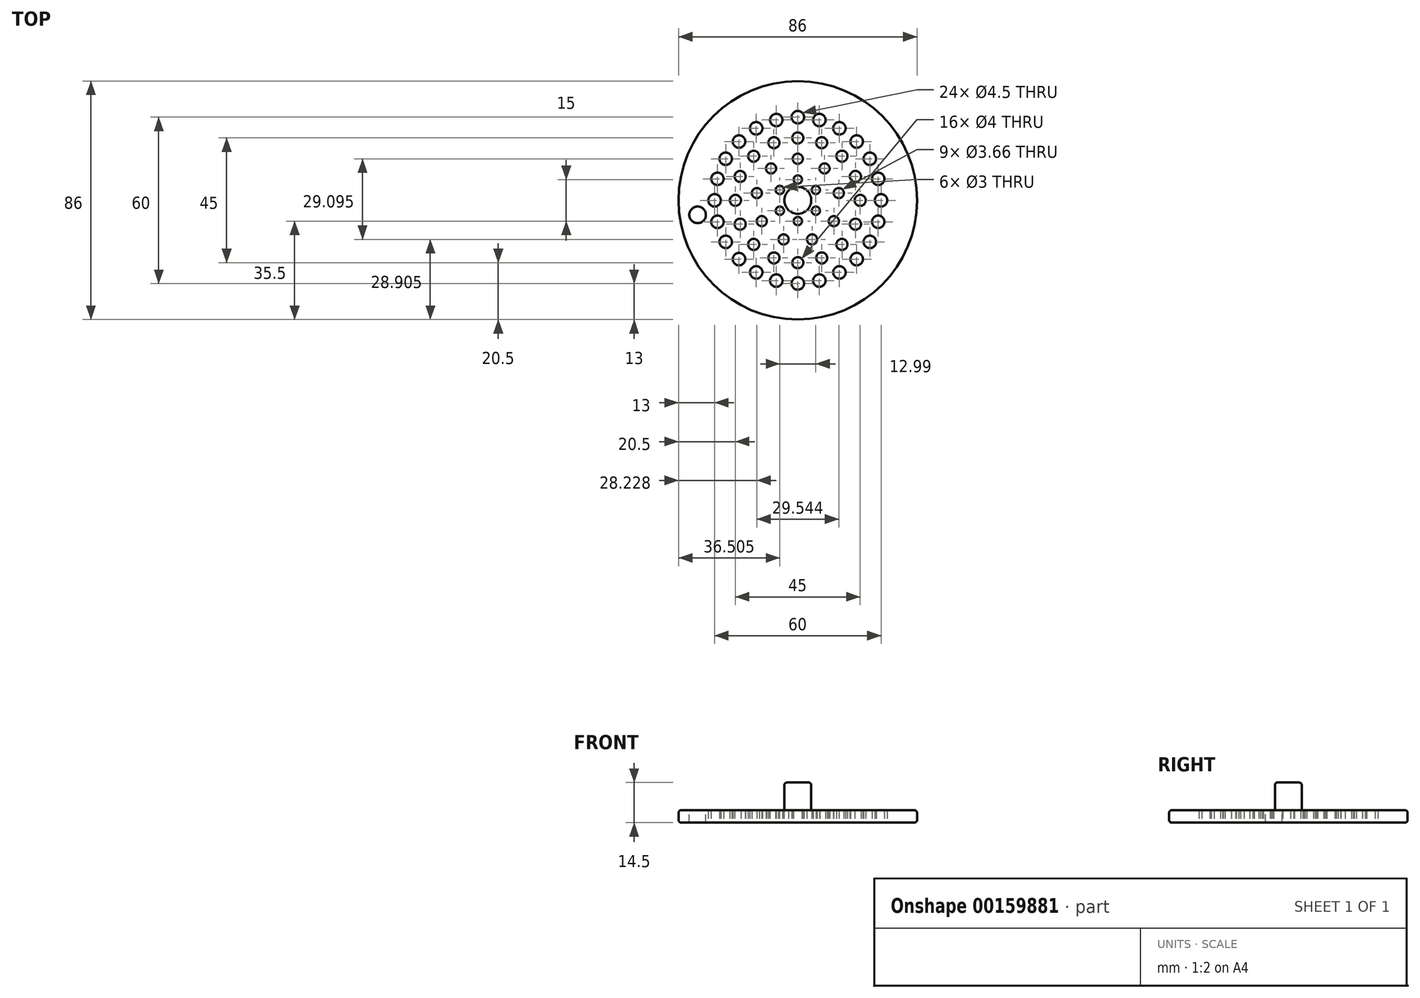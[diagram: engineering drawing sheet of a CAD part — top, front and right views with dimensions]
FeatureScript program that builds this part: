
annotation { "Feature Type Name" : "Feature", "Feature Type Description" : "" }
export const myFeature = defineFeature(function(context is Context, id is Id, definition is map)
    precondition{}
    {
        {
            var Q0;
            Q0=qCreatedBy(makeId("Top.planeOp"),FACE);
            var sketch = newSketch(context, id + "F0", { "sketchPlane" : qUnion([Q0])});
            skCircle(sketch, "E0", {"center": v(0, 0) * mm, "radius": 43 * mm});
            skSolve(sketch);
        }
        {
            var Q0;
            Q0=makeQuery(id+"F0.imprint","IMPRINT",FACE,{"disambiguationData":[TD([[makeQuery(id+"F0.imprint","IMPRINT",EDGE,{"derivedFrom":sQuery(id+"F0.wireOp",EDGE,"E0")}),1.0]])]});
            var sketch = newSketch(context, id + "F1", { "sketchPlane" : qUnion([Q0])});
            skCircle(sketch, "E1", {"center": v(0, 0) * mm, "radius": 7.5 * mm, "construction": true});
            skCircle(sketch, "E2", {"center": v(0, 7.5) * mm, "radius": 1.5 * mm});
            skCircle(sketch, "E3.1.1", {"center": v(-6.5, 3.75) * mm, "radius": 1.5 * mm});
            skCircle(sketch, "E3.2.1", {"center": v(-6.5, -3.75) * mm, "radius": 1.5 * mm});
            skCircle(sketch, "E3.3.1", {"center": v(0, -7.5) * mm, "radius": 1.5 * mm});
            skCircle(sketch, "E3.4.1", {"center": v(6.5, -3.75) * mm, "radius": 1.5 * mm});
            skCircle(sketch, "E3.5.1", {"center": v(6.5, 3.75) * mm, "radius": 1.5 * mm});
            skSolve(sketch);
        }
        {
            var Q0;
            Q0=makeQuery(id+"F0.imprint","IMPRINT",FACE,{"disambiguationData":[TD([[makeQuery(id+"F0.imprint","IMPRINT",EDGE,{"derivedFrom":sQuery(id+"F0.wireOp",EDGE,"E0")}),1.0]])]});
            var sketch = newSketch(context, id + "F2", { "sketchPlane" : qUnion([Q0])});
            skCircle(sketch, "E4", {"center": v(0, 0) * mm, "radius": 15 * mm, "construction": true});
            skCircle(sketch, "E5", {"center": v(0, 15) * mm, "radius": 1.83 * mm});
            skCircle(sketch, "E6.1.0", {"center": v(-9.64, 11.5) * mm, "radius": 1.83 * mm});
            skCircle(sketch, "E6.2.0", {"center": v(-14.77, 2.6) * mm, "radius": 1.83 * mm});
            skCircle(sketch, "E6.3.0", {"center": v(-13, -7.5) * mm, "radius": 1.83 * mm});
            skCircle(sketch, "E6.4.0", {"center": v(-5.13, -14.1) * mm, "radius": 1.83 * mm});
            skCircle(sketch, "E6.5.0", {"center": v(5.13, -14.1) * mm, "radius": 1.83 * mm});
            skCircle(sketch, "E6.6.0", {"center": v(13, -7.5) * mm, "radius": 1.83 * mm});
            skCircle(sketch, "E6.7.0", {"center": v(14.77, 2.6) * mm, "radius": 1.83 * mm});
            skCircle(sketch, "E6.8.0", {"center": v(9.64, 11.5) * mm, "radius": 1.83 * mm});
            skSolve(sketch);
        }
        {
            var Q0;
            Q0=makeQuery(id+"F0.imprint","IMPRINT",FACE,{"disambiguationData":[TD([[makeQuery(id+"F0.imprint","IMPRINT",EDGE,{"derivedFrom":sQuery(id+"F0.wireOp",EDGE,"E0")}),1.0]])]});
            var sketch = newSketch(context, id + "F3", { "sketchPlane" : qUnion([Q0])});
            skCircle(sketch, "E7", {"center": v(0, 0) * mm, "radius": 22.5 * mm, "construction": true});
            skCircle(sketch, "E8", {"center": v(0, 22.5) * mm, "radius": 2 * mm});
            skCircle(sketch, "E9.1.0", {"center": v(-8.61, 20.79) * mm, "radius": 2 * mm});
            skCircle(sketch, "E9.2.0", {"center": v(-15.9, 15.9) * mm, "radius": 2 * mm});
            skCircle(sketch, "E9.3.0", {"center": v(-20.79, 8.61) * mm, "radius": 2 * mm});
            skCircle(sketch, "E9.4.0", {"center": v(-22.5, 0) * mm, "radius": 2 * mm});
            skCircle(sketch, "E9.5.0", {"center": v(-20.79, -8.61) * mm, "radius": 2 * mm});
            skCircle(sketch, "E9.6.0", {"center": v(-15.9, -15.9) * mm, "radius": 2 * mm});
            skCircle(sketch, "E9.7.0", {"center": v(-8.61, -20.79) * mm, "radius": 2 * mm});
            skCircle(sketch, "E9.8.0", {"center": v(0, -22.5) * mm, "radius": 2 * mm});
            skCircle(sketch, "E9.9.0", {"center": v(8.61, -20.79) * mm, "radius": 2 * mm});
            skCircle(sketch, "E9.10.0", {"center": v(15.9, -15.9) * mm, "radius": 2 * mm});
            skCircle(sketch, "E9.11.0", {"center": v(20.79, -8.61) * mm, "radius": 2 * mm});
            skCircle(sketch, "E9.12.0", {"center": v(22.5, 0) * mm, "radius": 2 * mm});
            skCircle(sketch, "E9.13.0", {"center": v(20.79, 8.61) * mm, "radius": 2 * mm});
            skCircle(sketch, "E9.14.0", {"center": v(15.9, 15.9) * mm, "radius": 2 * mm});
            skCircle(sketch, "E9.15.0", {"center": v(8.61, 20.79) * mm, "radius": 2 * mm});
            skSolve(sketch);
        }
        {
            var Q0;
            Q0=makeQuery(id+"F0.imprint","IMPRINT",FACE,{"disambiguationData":[TD([[makeQuery(id+"F0.imprint","IMPRINT",EDGE,{"derivedFrom":sQuery(id+"F0.wireOp",EDGE,"E0")}),1.0]])]});
            var sketch = newSketch(context, id + "F4", { "sketchPlane" : qUnion([Q0])});
            skCircle(sketch, "E10", {"center": v(0, 0) * mm, "radius": 30 * mm, "construction": true});
            skCircle(sketch, "E11", {"center": v(0, 30) * mm, "radius": 2.25 * mm});
            skCircle(sketch, "E12.1.0", {"center": v(-7.76, 28.98) * mm, "radius": 2.25 * mm});
            skCircle(sketch, "E12.2.0", {"center": v(-15, 25.98) * mm, "radius": 2.25 * mm});
            skCircle(sketch, "E13.1.3.0", {"center": v(-21.21, 21.21) * mm, "radius": 2.25 * mm});
            skCircle(sketch, "E13.1.4.0", {"center": v(-25.98, 15) * mm, "radius": 2.25 * mm});
            skCircle(sketch, "E13.1.5.0", {"center": v(-28.98, 7.76) * mm, "radius": 2.25 * mm});
            skCircle(sketch, "E13.1.6.0", {"center": v(-30, 0) * mm, "radius": 2.25 * mm});
            skCircle(sketch, "E13.1.7.0", {"center": v(-28.98, -7.76) * mm, "radius": 2.25 * mm});
            skCircle(sketch, "E13.1.8.0", {"center": v(-25.98, -15) * mm, "radius": 2.25 * mm});
            skCircle(sketch, "E13.1.9.0", {"center": v(-21.21, -21.21) * mm, "radius": 2.25 * mm});
            skCircle(sketch, "E13.1.10.0", {"center": v(-15, -25.98) * mm, "radius": 2.25 * mm});
            skCircle(sketch, "E13.1.11.0", {"center": v(-7.76, -28.98) * mm, "radius": 2.25 * mm});
            skCircle(sketch, "E13.1.12.0", {"center": v(0, -30) * mm, "radius": 2.25 * mm});
            skCircle(sketch, "E13.1.13.0", {"center": v(7.76, -28.98) * mm, "radius": 2.25 * mm});
            skCircle(sketch, "E13.1.14.0", {"center": v(15, -25.98) * mm, "radius": 2.25 * mm});
            skCircle(sketch, "E13.1.15.0", {"center": v(21.21, -21.21) * mm, "radius": 2.25 * mm});
            skCircle(sketch, "E13.1.16.0", {"center": v(25.98, -15) * mm, "radius": 2.25 * mm});
            skCircle(sketch, "E13.1.17.0", {"center": v(28.98, -7.76) * mm, "radius": 2.25 * mm});
            skCircle(sketch, "E13.1.18.0", {"center": v(30, 0) * mm, "radius": 2.25 * mm});
            skCircle(sketch, "E13.1.19.0", {"center": v(28.98, 7.76) * mm, "radius": 2.25 * mm});
            skCircle(sketch, "E13.1.20.0", {"center": v(25.98, 15) * mm, "radius": 2.25 * mm});
            skCircle(sketch, "E13.1.21.0", {"center": v(21.21, 21.21) * mm, "radius": 2.25 * mm});
            skCircle(sketch, "E13.1.22.0", {"center": v(15, 25.98) * mm, "radius": 2.25 * mm});
            skCircle(sketch, "E13.1.23.0", {"center": v(7.76, 28.98) * mm, "radius": 2.25 * mm});
            skSolve(sketch);
        }
        {
            var Q0;
            Q0=qSketchRegion(id+"F4",true);
            extrude(context, id + "F5", {"entities" : qUnion([Q0]), "depth" : 5 * mm});
        }
        {
            var Q0;
            Q0=qSketchRegion(id+"F3",true);
            extrude(context, id + "F6", {"entities" : qUnion([Q0]), "depth" : 5 * mm});
        }
        {
            var Q0;
            Q0=qSketchRegion(id+"F2",true);
            extrude(context, id + "F7", {"entities" : qUnion([Q0]), "depth" : 5 * mm});
        }
        {
            var Q0;
            Q0=qSketchRegion(id+"F1",true);
            extrude(context, id + "F8", {"entities" : qUnion([Q0]), "depth" : 5 * mm});
        }
        {
            var Q0;
            Q0=qSketchRegion(id+"F0",true);
            extrude(context, id + "F9", {"entities" : qUnion([Q0]), "depth" : 4.5 * mm});
        }
        {
            var Q0;
            Q0=makeQuery(id+"F5.opExtrude","SWEPT_BODY",BODY,{"disambiguationData":[OSD([sQuery(id+"F4.wireOp",EDGE,"E11")])]});
            var Q1;
            Q1=makeQuery(id+"F5.opExtrude","SWEPT_BODY",BODY,{"disambiguationData":[OSD([sQuery(id+"F4.wireOp",EDGE,"E13.1.3.0")])]});
            var Q2;
            Q2=makeQuery(id+"F5.opExtrude","SWEPT_BODY",BODY,{"disambiguationData":[OSD([sQuery(id+"F4.wireOp",EDGE,"E13.1.7.0")])]});
            var Q3;
            Q3=makeQuery(id+"F5.opExtrude","SWEPT_BODY",BODY,{"disambiguationData":[OSD([sQuery(id+"F4.wireOp",EDGE,"E12.1.0")])]});
            var Q4;
            Q4=makeQuery(id+"F5.opExtrude","SWEPT_BODY",BODY,{"disambiguationData":[OSD([sQuery(id+"F4.wireOp",EDGE,"E12.2.0")])]});
            var Q5;
            Q5=makeQuery(id+"F5.opExtrude","SWEPT_BODY",BODY,{"disambiguationData":[OSD([sQuery(id+"F4.wireOp",EDGE,"E13.1.4.0")])]});
            var Q6;
            Q6=makeQuery(id+"F5.opExtrude","SWEPT_BODY",BODY,{"disambiguationData":[OSD([sQuery(id+"F4.wireOp",EDGE,"E13.1.5.0")])]});
            var Q7;
            Q7=makeQuery(id+"F5.opExtrude","SWEPT_BODY",BODY,{"disambiguationData":[OSD([sQuery(id+"F4.wireOp",EDGE,"E13.1.6.0")])]});
            var Q8;
            Q8=makeQuery(id+"F5.opExtrude","SWEPT_BODY",BODY,{"disambiguationData":[OSD([sQuery(id+"F4.wireOp",EDGE,"E13.1.8.0")])]});
            var Q9;
            Q9=makeQuery(id+"F5.opExtrude","SWEPT_BODY",BODY,{"disambiguationData":[OSD([sQuery(id+"F4.wireOp",EDGE,"E13.1.9.0")])]});
            var Q10;
            Q10=makeQuery(id+"F5.opExtrude","SWEPT_BODY",BODY,{"disambiguationData":[OSD([sQuery(id+"F4.wireOp",EDGE,"E13.1.10.0")])]});
            var Q11;
            Q11=makeQuery(id+"F5.opExtrude","SWEPT_BODY",BODY,{"disambiguationData":[OSD([sQuery(id+"F4.wireOp",EDGE,"E13.1.11.0")])]});
            var Q12;
            Q12=makeQuery(id+"F5.opExtrude","SWEPT_BODY",BODY,{"disambiguationData":[OSD([sQuery(id+"F4.wireOp",EDGE,"E13.1.12.0")])]});
            var Q13;
            Q13=makeQuery(id+"F5.opExtrude","SWEPT_BODY",BODY,{"disambiguationData":[OSD([sQuery(id+"F4.wireOp",EDGE,"E13.1.13.0")])]});
            var Q14;
            Q14=makeQuery(id+"F5.opExtrude","SWEPT_BODY",BODY,{"disambiguationData":[OSD([sQuery(id+"F4.wireOp",EDGE,"E13.1.14.0")])]});
            var Q15;
            Q15=makeQuery(id+"F5.opExtrude","SWEPT_BODY",BODY,{"disambiguationData":[OSD([sQuery(id+"F4.wireOp",EDGE,"E13.1.15.0")])]});
            var Q16;
            Q16=makeQuery(id+"F5.opExtrude","SWEPT_BODY",BODY,{"disambiguationData":[OSD([sQuery(id+"F4.wireOp",EDGE,"E13.1.16.0")])]});
            var Q17;
            Q17=makeQuery(id+"F5.opExtrude","SWEPT_BODY",BODY,{"disambiguationData":[OSD([sQuery(id+"F4.wireOp",EDGE,"E13.1.17.0")])]});
            var Q18;
            Q18=makeQuery(id+"F5.opExtrude","SWEPT_BODY",BODY,{"disambiguationData":[OSD([sQuery(id+"F4.wireOp",EDGE,"E13.1.18.0")])]});
            var Q19;
            Q19=makeQuery(id+"F5.opExtrude","SWEPT_BODY",BODY,{"disambiguationData":[OSD([sQuery(id+"F4.wireOp",EDGE,"E13.1.19.0")])]});
            var Q20;
            Q20=makeQuery(id+"F5.opExtrude","SWEPT_BODY",BODY,{"disambiguationData":[OSD([sQuery(id+"F4.wireOp",EDGE,"E13.1.20.0")])]});
            var Q21;
            Q21=makeQuery(id+"F5.opExtrude","SWEPT_BODY",BODY,{"disambiguationData":[OSD([sQuery(id+"F4.wireOp",EDGE,"E13.1.21.0")])]});
            var Q22;
            Q22=makeQuery(id+"F5.opExtrude","SWEPT_BODY",BODY,{"disambiguationData":[OSD([sQuery(id+"F4.wireOp",EDGE,"E13.1.22.0")])]});
            var Q23;
            Q23=makeQuery(id+"F5.opExtrude","SWEPT_BODY",BODY,{"disambiguationData":[OSD([sQuery(id+"F4.wireOp",EDGE,"E13.1.23.0")])]});
            var Q24;
            Q24=makeQuery(id+"F6.opExtrude","SWEPT_BODY",BODY,{"disambiguationData":[OSD([sQuery(id+"F3.wireOp",EDGE,"E9.15.0")])]});
            var Q25;
            Q25=makeQuery(id+"F6.opExtrude","SWEPT_BODY",BODY,{"disambiguationData":[OSD([sQuery(id+"F3.wireOp",EDGE,"E8")])]});
            var Q26;
            Q26=makeQuery(id+"F6.opExtrude","SWEPT_BODY",BODY,{"disambiguationData":[OSD([sQuery(id+"F3.wireOp",EDGE,"E9.1.0")])]});
            var Q27;
            Q27=makeQuery(id+"F6.opExtrude","SWEPT_BODY",BODY,{"disambiguationData":[OSD([sQuery(id+"F3.wireOp",EDGE,"E9.2.0")])]});
            var Q28;
            Q28=makeQuery(id+"F6.opExtrude","SWEPT_BODY",BODY,{"disambiguationData":[OSD([sQuery(id+"F3.wireOp",EDGE,"E9.3.0")])]});
            var Q29;
            Q29=makeQuery(id+"F6.opExtrude","SWEPT_BODY",BODY,{"disambiguationData":[OSD([sQuery(id+"F3.wireOp",EDGE,"E9.4.0")])]});
            var Q30;
            Q30=makeQuery(id+"F6.opExtrude","SWEPT_BODY",BODY,{"disambiguationData":[OSD([sQuery(id+"F3.wireOp",EDGE,"E9.5.0")])]});
            var Q31;
            Q31=makeQuery(id+"F6.opExtrude","SWEPT_BODY",BODY,{"disambiguationData":[OSD([sQuery(id+"F3.wireOp",EDGE,"E9.6.0")])]});
            var Q32;
            Q32=makeQuery(id+"F6.opExtrude","SWEPT_BODY",BODY,{"disambiguationData":[OSD([sQuery(id+"F3.wireOp",EDGE,"E9.7.0")])]});
            var Q33;
            Q33=makeQuery(id+"F6.opExtrude","SWEPT_BODY",BODY,{"disambiguationData":[OSD([sQuery(id+"F3.wireOp",EDGE,"E9.8.0")])]});
            var Q34;
            Q34=makeQuery(id+"F6.opExtrude","SWEPT_BODY",BODY,{"disambiguationData":[OSD([sQuery(id+"F3.wireOp",EDGE,"E9.9.0")])]});
            var Q35;
            Q35=makeQuery(id+"F6.opExtrude","SWEPT_BODY",BODY,{"disambiguationData":[OSD([sQuery(id+"F3.wireOp",EDGE,"E9.10.0")])]});
            var Q36;
            Q36=makeQuery(id+"F6.opExtrude","SWEPT_BODY",BODY,{"disambiguationData":[OSD([sQuery(id+"F3.wireOp",EDGE,"E9.11.0")])]});
            var Q37;
            Q37=makeQuery(id+"F6.opExtrude","SWEPT_BODY",BODY,{"disambiguationData":[OSD([sQuery(id+"F3.wireOp",EDGE,"E9.12.0")])]});
            var Q38;
            Q38=makeQuery(id+"F6.opExtrude","SWEPT_BODY",BODY,{"disambiguationData":[OSD([sQuery(id+"F3.wireOp",EDGE,"E9.13.0")])]});
            var Q39;
            Q39=makeQuery(id+"F6.opExtrude","SWEPT_BODY",BODY,{"disambiguationData":[OSD([sQuery(id+"F3.wireOp",EDGE,"E9.14.0")])]});
            var Q40;
            Q40=makeQuery(id+"F7.opExtrude","SWEPT_BODY",BODY,{"disambiguationData":[OSD([sQuery(id+"F2.wireOp",EDGE,"E6.8.0")])]});
            var Q41;
            Q41=makeQuery(id+"F7.opExtrude","SWEPT_BODY",BODY,{"disambiguationData":[OSD([sQuery(id+"F2.wireOp",EDGE,"E6.7.0")])]});
            var Q42;
            Q42=makeQuery(id+"F7.opExtrude","SWEPT_BODY",BODY,{"disambiguationData":[OSD([sQuery(id+"F2.wireOp",EDGE,"E6.6.0")])]});
            var Q43;
            Q43=makeQuery(id+"F7.opExtrude","SWEPT_BODY",BODY,{"disambiguationData":[OSD([sQuery(id+"F2.wireOp",EDGE,"E6.5.0")])]});
            var Q44;
            Q44=makeQuery(id+"F7.opExtrude","SWEPT_BODY",BODY,{"disambiguationData":[OSD([sQuery(id+"F2.wireOp",EDGE,"E6.4.0")])]});
            var Q45;
            Q45=makeQuery(id+"F7.opExtrude","SWEPT_BODY",BODY,{"disambiguationData":[OSD([sQuery(id+"F2.wireOp",EDGE,"E6.3.0")])]});
            var Q46;
            Q46=makeQuery(id+"F7.opExtrude","SWEPT_BODY",BODY,{"disambiguationData":[OSD([sQuery(id+"F2.wireOp",EDGE,"E6.2.0")])]});
            var Q47;
            Q47=makeQuery(id+"F7.opExtrude","SWEPT_BODY",BODY,{"disambiguationData":[OSD([sQuery(id+"F2.wireOp",EDGE,"E6.1.0")])]});
            var Q48;
            Q48=makeQuery(id+"F7.opExtrude","SWEPT_BODY",BODY,{"disambiguationData":[OSD([sQuery(id+"F2.wireOp",EDGE,"E5")])]});
            var Q49;
            Q49=makeQuery(id+"F8.opExtrude","SWEPT_BODY",BODY,{"disambiguationData":[OSD([sQuery(id+"F1.wireOp",EDGE,"E2")])]});
            var Q50;
            Q50=makeQuery(id+"F8.opExtrude","SWEPT_BODY",BODY,{"disambiguationData":[OSD([sQuery(id+"F1.wireOp",EDGE,"E3.5.1")])]});
            var Q51;
            Q51=makeQuery(id+"F8.opExtrude","SWEPT_BODY",BODY,{"disambiguationData":[OSD([sQuery(id+"F1.wireOp",EDGE,"E3.4.1")])]});
            var Q52;
            Q52=makeQuery(id+"F8.opExtrude","SWEPT_BODY",BODY,{"disambiguationData":[OSD([sQuery(id+"F1.wireOp",EDGE,"E3.3.1")])]});
            var Q53;
            Q53=makeQuery(id+"F8.opExtrude","SWEPT_BODY",BODY,{"disambiguationData":[OSD([sQuery(id+"F1.wireOp",EDGE,"E3.2.1")])]});
            var Q54;
            Q54=makeQuery(id+"F8.opExtrude","SWEPT_BODY",BODY,{"disambiguationData":[OSD([sQuery(id+"F1.wireOp",EDGE,"E3.1.1")])]});
            var Q55;
            Q55=makeQuery(id+"F9.opExtrude","SWEPT_BODY",BODY,{"disambiguationData":[OSD([sQuery(id+"F0.wireOp",EDGE,"E0")])]});
            booleanBodies(context, id + "F10", {"operationType" : BooleanOperationType.SUBTRACTION, "tools" : qUnion([Q0, Q1, Q2, Q3, Q4, Q5, Q6, Q7, Q8, Q9, Q10, Q11, Q12, Q13, Q14, Q15, Q16, Q17, Q18, Q19, Q20, Q21, Q22, Q23, Q24, Q25, Q26, Q27, Q28, Q29, Q30, Q31, Q32, Q33, Q34, Q35, Q36, Q37, Q38, Q39, Q40, Q41, Q42, Q43, Q44, Q45, Q46, Q47, Q48, Q49, Q50, Q51, Q52, Q53, Q54]), "targets" : qUnion([Q55])});
        }
        {
            var Q0;
            Q0=makeQuery(id+"F9.opExtrude","CAP_EDGE",EDGE,{"disambiguationData":[OSD([sQuery(id+"F0.wireOp",EDGE,"E0")])],"isStart":true});
            var Q1;
            Q1=makeQuery(id+"F9.opExtrude","CAP_EDGE",EDGE,{"disambiguationData":[OSD([sQuery(id+"F0.wireOp",EDGE,"E0")])],"isStart":false});
            fillet(context, id + "F11", {"entities" : qUnion([Q0, Q1]), "radius" : 1 * mm, "tangentPropagation" : true, "allowEdgeOverflow" : false});
        }
        {
            var Q0;
            Q0=makeQuery(id+"F9.opExtrude","CAP_FACE",FACE,{"disambiguationData":[OSD([sQuery(id+"F0.wireOp",EDGE,"E0")])],"isStart":false});
            var sketch = newSketch(context, id + "F12", { "sketchPlane" : qUnion([Q0])});
            skCircle(sketch, "E14", {"center": v(0, 0) * mm, "radius": 4.85 * mm});
            skSolve(sketch);
        }
        {
            var Q0;
            Q0=makeQuery(id+"F12.imprint","IMPRINT",FACE,{"disambiguationData":[TD([[makeQuery(id+"F12.imprint","IMPRINT",EDGE,{"derivedFrom":sQuery(id+"F12.wireOp",EDGE,"E14")}),1.0]])]});
            extrude(context, id + "F13", {"entities" : qUnion([Q0]), "operationType" : NewBodyOperationType.ADD, "depth" : 10 * mm});
        }
        {
            var Q0;
            Q0=makeQuery(id+"F13.opExtrude","CAP_EDGE",EDGE,{"disambiguationData":[OSD([sQuery(id+"F12.wireOp",EDGE,"E14")])],"isStart":false});
            fillet(context, id + "F14", {"entities" : qUnion([Q0]), "radius" : 1 * mm, "tangentPropagation" : true, "allowEdgeOverflow" : false});
        }
        {
            var Q0;
            Q0=makeQuery(id+"F9.opExtrude","CAP_FACE",FACE,{"disambiguationData":[OSD([sQuery(id+"F0.wireOp",EDGE,"E0")])],"isStart":false});
            var sketch = newSketch(context, id + "F15", { "sketchPlane" : qUnion([Q0])});
            skCircle(sketch, "E15", {"center": v(0, 0) * mm, "radius": 36.5 * mm, "construction": true});
            skCircle(sketch, "E16", {"center": v(-36.12, -5.23) * mm, "radius": 3 * mm});
            skSolve(sketch);
        }
        {
            var Q0;
            Q0=makeQuery(id+"F15.imprint","IMPRINT",FACE,{"disambiguationData":[TD([[makeQuery(id+"F15.imprint","IMPRINT",EDGE,{"derivedFrom":sQuery(id+"F15.wireOp",EDGE,"E16")}),1.0]])]});
            extrude(context, id + "F16", {"entities" : qUnion([Q0]), "operationType" : NewBodyOperationType.REMOVE, "oppositeDirection" : true, "depth" : 25 * mm});
        }
    });
